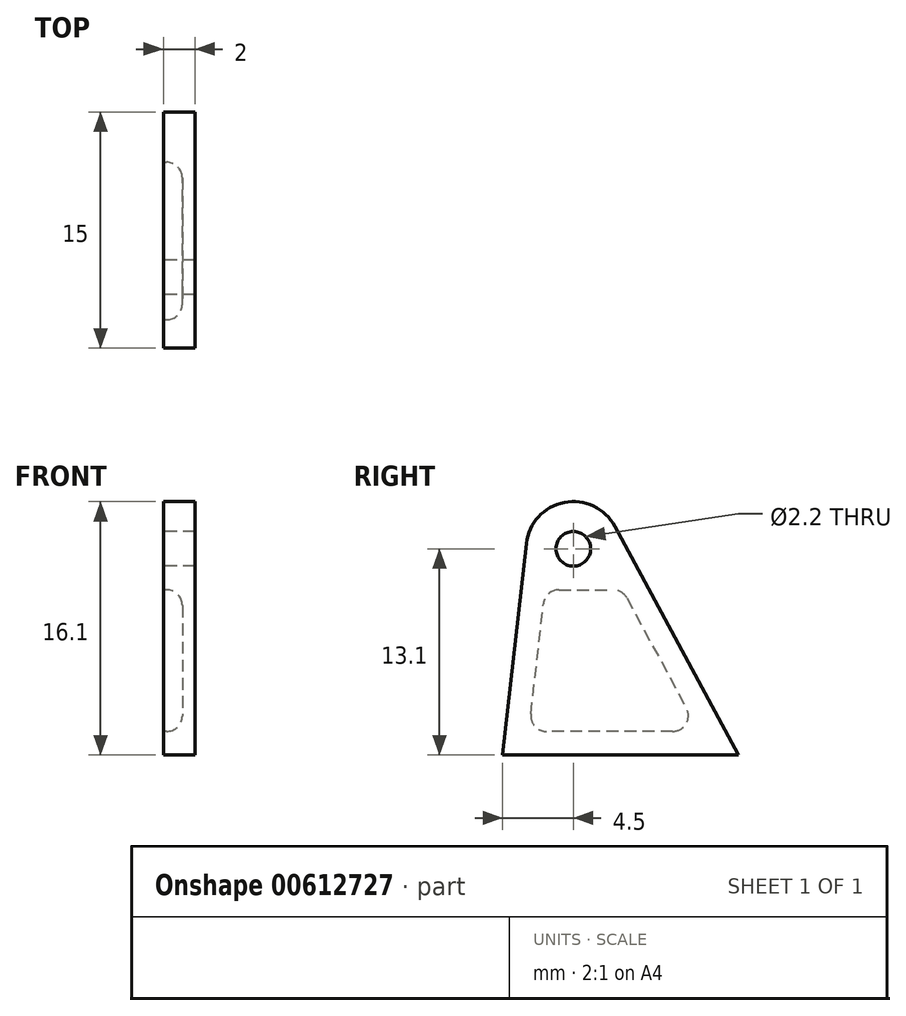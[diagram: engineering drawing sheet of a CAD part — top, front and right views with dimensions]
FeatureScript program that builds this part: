
annotation { "Feature Type Name" : "Feature", "Feature Type Description" : "" }
export const myFeature = defineFeature(function(context is Context, id is Id, definition is map)
    precondition{}
    {
        {
            var Q0;
            Q0=qCreatedBy(makeId("Right.planeOp"),FACE);
            var sketch = newSketch(context, id + "F0", { "sketchPlane" : qUnion([Q0])});
            skCircle(sketch, "E0", {"center": v(0, 13.1) * mm, "radius": 1.1 * mm});
            skLineSegment(sketch, "E1", {"start": v(10.5, 0) * mm, "end": v(2.64, 14.53) * mm});
            skLineSegment(sketch, "E2", {"start": v(10.5, 0) * mm, "end": v(-4.5, 0) * mm});
            skLineSegment(sketch, "E3", {"start": v(-4.5, 0) * mm, "end": v(-2.98, 13.44) * mm});
            skArc(sketch, "E4", {"start": v(2.64, 14.53) * mm, "mid": v(-0.57, 16.05) * mm, "end": v(-2.98, 13.44) * mm});
            skSolve(sketch);
        }
        {
            var Q0;
            Q0=qSketchRegion(id+"F0",true);
            extrude(context, id + "F1", {"entities" : qUnion([Q0]), "depth" : 2 * mm, "offsetDistance" : 25 * mm});
        }
        {
            var Q0;
            Q0=makeQuery(id+"F1.opExtrude","CAP_FACE",FACE,{"disambiguationData":[OSD([sQuery(id+"F0.wireOp",EDGE,"E0"),sQuery(id+"F0.wireOp",EDGE,"E1"),sQuery(id+"F0.wireOp",EDGE,"E2"),sQuery(id+"F0.wireOp",EDGE,"E3"),sQuery(id+"F0.wireOp",EDGE,"E4")])],"isStart":true});
            var sketch = newSketch(context, id + "F2", { "sketchPlane" : qUnion([Q0])});
            skLineSegment(sketch, "E5", {"start": v(-7.98, 1.5) * mm, "end": v(2.82, 1.5) * mm});
            skLineSegment(sketch, "E6", {"start": v(2.82, 1.5) * mm, "end": v(1.8, 10.5) * mm});
            skLineSegment(sketch, "E7", {"start": v(1.8, 10.5) * mm, "end": v(-3.11, 10.5) * mm});
            skLineSegment(sketch, "E8", {"start": v(-3.11, 10.5) * mm, "end": v(-7.98, 1.5) * mm});
            skSolve(sketch);
        }
        {
            var Q0;
            Q0=qSketchRegion(id+"F2",true);
            extrude(context, id + "F3", {"entities" : qUnion([Q0]), "operationType" : NewBodyOperationType.REMOVE, "oppositeDirection" : true, "depth" : 1.2 * mm, "offsetDistance" : 25 * mm});
        }
        {
            var Q0;
            Q0=makeQuery(id+"F3.boolean.opBoolean","COPY",EDGE,{"derivedFrom":makeQuery(id+"F3.opExtrude","SWEPT_EDGE",EDGE,{"disambiguationData":[OSD([sQuery(id+"F2.wireOp",EDGE,"E7"),sQuery(id+"F2.wireOp",EDGE,"E8")])]})});
            var Q1;
            Q1=makeQuery(id+"F3.boolean.opBoolean","COPY",EDGE,{"derivedFrom":makeQuery(id+"F3.opExtrude","SWEPT_EDGE",EDGE,{"disambiguationData":[OSD([sQuery(id+"F2.wireOp",EDGE,"E6"),sQuery(id+"F2.wireOp",EDGE,"E7")])]})});
            var Q2;
            Q2=makeQuery(id+"F3.boolean.opBoolean","COPY",EDGE,{"derivedFrom":makeQuery(id+"F3.opExtrude","SWEPT_EDGE",EDGE,{"disambiguationData":[OSD([sQuery(id+"F2.wireOp",EDGE,"E5"),sQuery(id+"F2.wireOp",EDGE,"E6")])]})});
            var Q3;
            Q3=makeQuery(id+"F3.boolean.opBoolean","COPY",EDGE,{"derivedFrom":makeQuery(id+"F3.opExtrude","SWEPT_EDGE",EDGE,{"disambiguationData":[OSD([sQuery(id+"F2.wireOp",EDGE,"E5"),sQuery(id+"F2.wireOp",EDGE,"E8")])]})});
            var Q4;
            Q4=makeQuery(id+"F3.boolean.opBoolean","COPY",FACE,{"derivedFrom":makeQuery(id+"F3.opExtrude","CAP_FACE",FACE,{"disambiguationData":[OSD([sQuery(id+"F2.wireOp",EDGE,"E5"),sQuery(id+"F2.wireOp",EDGE,"E6"),sQuery(id+"F2.wireOp",EDGE,"E7"),sQuery(id+"F2.wireOp",EDGE,"E8")])],"isStart":false})});
            fillet(context, id + "F4", {"entities" : qUnion([Q0, Q1, Q2, Q3, Q4]), "radius" : 1 * mm, "tangentPropagation" : true, "allowEdgeOverflow" : false});
        }
    });
